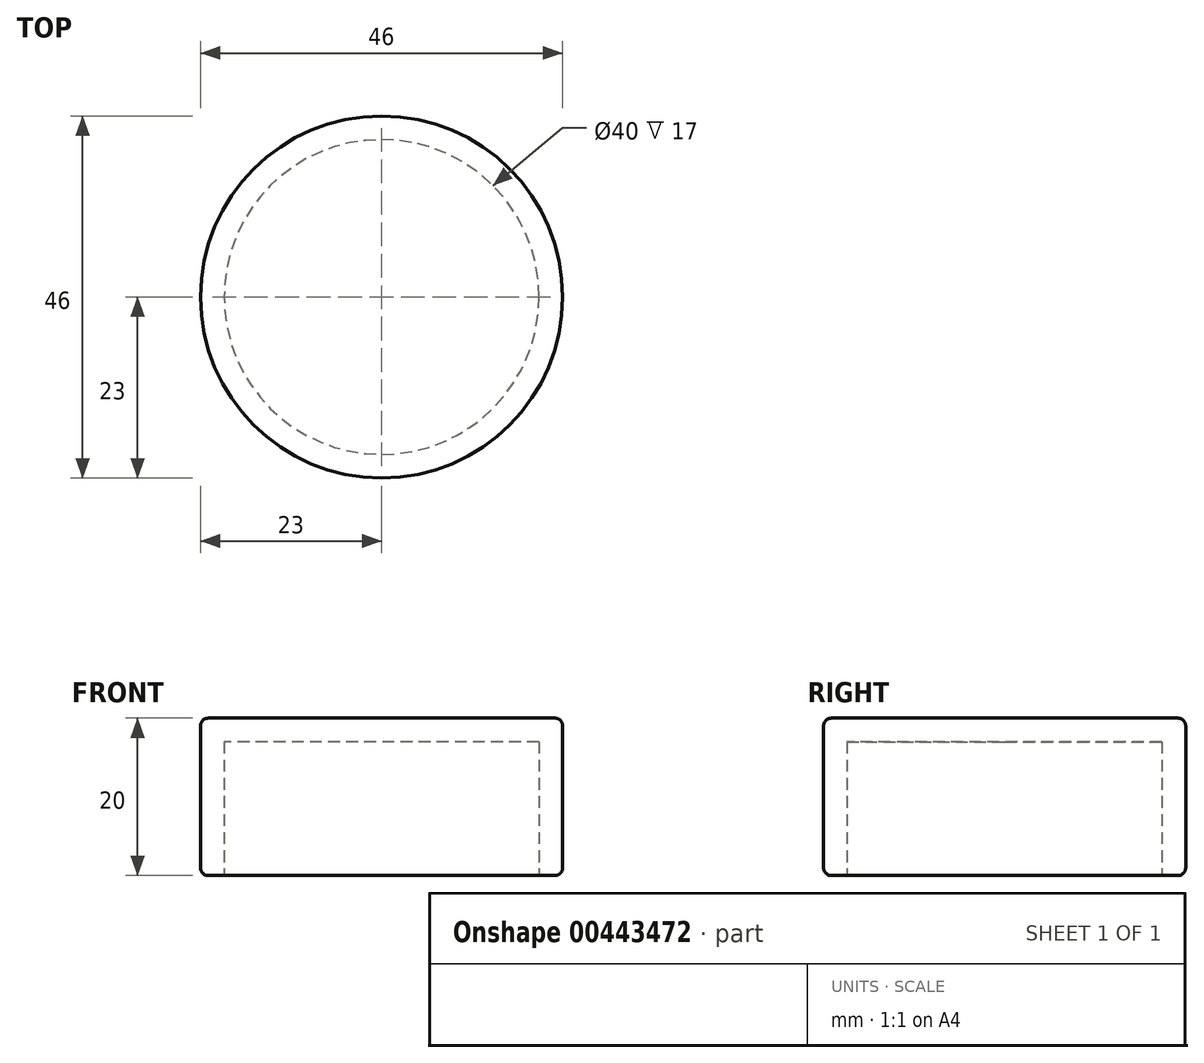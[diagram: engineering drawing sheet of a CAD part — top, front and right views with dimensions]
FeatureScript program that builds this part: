
annotation { "Feature Type Name" : "Feature", "Feature Type Description" : "" }
export const myFeature = defineFeature(function(context is Context, id is Id, definition is map)
    precondition{}
    {
        {
            var Q0;
            Q0=qCreatedBy(makeId("Top.planeOp"),FACE);
            var sketch = newSketch(context, id + "F0", { "sketchPlane" : qUnion([Q0])});
            skCircle(sketch, "E0", {"center": v(0, 0) * mm, "radius": 23 * mm});
            skCircle(sketch, "E1", {"center": v(0, 0) * mm, "radius": 20 * mm});
            skSolve(sketch);
        }
        {
            var Q0;
            Q0=makeQuery(id+"F0.imprint","IMPRINT",FACE,{"disambiguationData":[TD([[makeQuery(id+"F0.imprint","IMPRINT",EDGE,{"derivedFrom":sQuery(id+"F0.wireOp",EDGE,"E0")}),1.0]])]});
            extrude(context, id + "F1", {"entities" : qUnion([Q0]), "depth" : 20 * mm});
        }
        {
            var Q0;
            Q0=makeQuery(id+"F1.opExtrude","CAP_FACE",FACE,{"disambiguationData":[OSD([sQuery(id+"F0.wireOp",EDGE,"E0"),sQuery(id+"F0.wireOp",EDGE,"E1")])],"isStart":false});
            var sketch = newSketch(context, id + "F2", { "sketchPlane" : qUnion([Q0])});
            skCircle(sketch, "E2", {"center": v(0, 0) * mm, "radius": 23 * mm});
            skSolve(sketch);
        }
        {
            var Q0;
            Q0=makeQuery(id+"F2.imprint","IMPRINT",FACE,{"disambiguationData":[TD([[makeQuery(id+"F2.imprint","IMPRINT",EDGE,{"derivedFrom":makeQuery(id+"F1.opExtrude","CAP_EDGE",EDGE,{"disambiguationData":[OSD([sQuery(id+"F0.wireOp",EDGE,"E1")])],"isStart":false})}),1.0]])]});
            extrude(context, id + "F3", {"entities" : qUnion([Q0]), "operationType" : NewBodyOperationType.ADD, "oppositeDirection" : true, "depth" : 3 * mm});
        }
        {
            var Q0;
            Q0=makeQuery(id+"F1.opExtrude","CAP_EDGE",EDGE,{"disambiguationData":[OSD([sQuery(id+"F0.wireOp",EDGE,"E0")])],"isStart":true});
            var Q1;
            Q1=makeQuery(id+"F1.opExtrude","CAP_EDGE",EDGE,{"disambiguationData":[OSD([sQuery(id+"F0.wireOp",EDGE,"E0")])],"isStart":false});
            fillet(context, id + "F4", {"entities" : qUnion([Q0, Q1]), "radius" : 1 * mm, "tangentPropagation" : true, "allowEdgeOverflow" : false});
        }
    });
